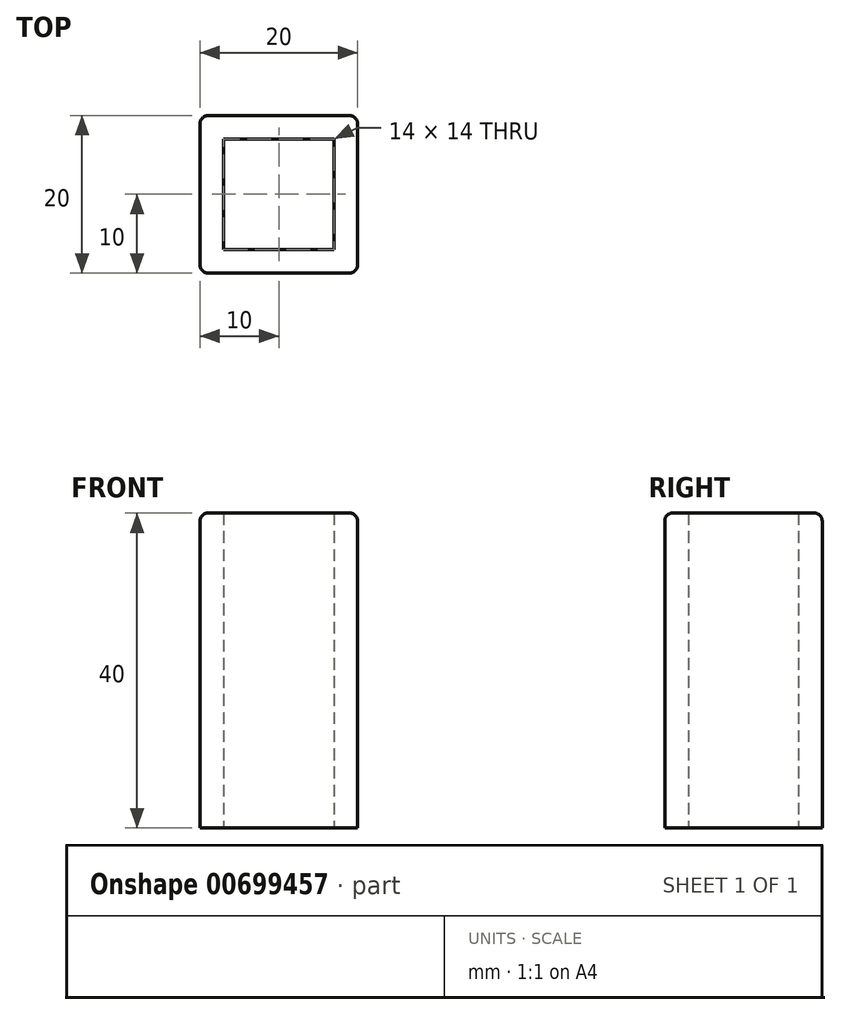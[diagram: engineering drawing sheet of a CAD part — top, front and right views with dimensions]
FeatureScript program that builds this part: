
annotation { "Feature Type Name" : "Feature", "Feature Type Description" : "" }
export const myFeature = defineFeature(function(context is Context, id is Id, definition is map)
    precondition{}
    {
        {
            var Q0;
            Q0=qCreatedBy(makeId("Top.planeOp"),FACE);
            var sketch = newSketch(context, id + "F0", { "sketchPlane" : qUnion([Q0])});
            skLineSegment(sketch, "E0.bottom", {"start": v(10, 10) * mm, "end": v(-10, 10) * mm});
            skLineSegment(sketch, "E0.top", {"start": v(10, -10) * mm, "end": v(-10, -10) * mm});
            skLineSegment(sketch, "E0.left", {"start": v(10, 10) * mm, "end": v(10, -10) * mm});
            skLineSegment(sketch, "E0.right", {"start": v(-10, 10) * mm, "end": v(-10, -10) * mm});
            skPoint(sketch, "E0.middle", {"position": v(0, 0) * mm});
            skLineSegment(sketch, "E1.0", {"start": v(7, -7) * mm, "end": v(-7, -7) * mm});
            skLineSegment(sketch, "E1.1", {"start": v(7, 7) * mm, "end": v(7, -7) * mm});
            skLineSegment(sketch, "E1.2", {"start": v(7, 7) * mm, "end": v(-7, 7) * mm});
            skLineSegment(sketch, "E1.3", {"start": v(-7, 7) * mm, "end": v(-7, -7) * mm});
            skSolve(sketch);
        }
        {
            var Q0;
            Q0=qSketchRegion(id+"F0",true);
            extrude(context, id + "F1", {"entities" : qUnion([Q0]), "depth" : 40 * mm, "offsetDistance" : 25 * mm});
        }
        {
            var Q0;
            Q0=makeQuery(id+"F1.opExtrude","SWEPT_EDGE",EDGE,{"disambiguationData":[OSD([sQuery(id+"F0.wireOp",EDGE,"E0.top"),sQuery(id+"F0.wireOp",EDGE,"E0.right")])]});
            var Q1;
            Q1=makeQuery(id+"F1.opExtrude","CAP_EDGE",EDGE,{"disambiguationData":[OSD([sQuery(id+"F0.wireOp",EDGE,"E0.top")])],"isStart":false});
            var Q2;
            Q2=makeQuery(id+"F1.opExtrude","CAP_EDGE",EDGE,{"disambiguationData":[OSD([sQuery(id+"F0.wireOp",EDGE,"E0.left")])],"isStart":false});
            var Q3;
            Q3=makeQuery(id+"F1.opExtrude","SWEPT_EDGE",EDGE,{"disambiguationData":[OSD([sQuery(id+"F0.wireOp",EDGE,"E0.top"),sQuery(id+"F0.wireOp",EDGE,"E0.left")])]});
            var Q4;
            Q4=makeQuery(id+"F1.opExtrude","SWEPT_EDGE",EDGE,{"disambiguationData":[OSD([sQuery(id+"F0.wireOp",EDGE,"E0.bottom"),sQuery(id+"F0.wireOp",EDGE,"E0.left")])]});
            var Q5;
            Q5=makeQuery(id+"F1.opExtrude","CAP_EDGE",EDGE,{"disambiguationData":[OSD([sQuery(id+"F0.wireOp",EDGE,"E0.bottom")])],"isStart":false});
            var Q6;
            Q6=makeQuery(id+"F1.opExtrude","CAP_EDGE",EDGE,{"disambiguationData":[OSD([sQuery(id+"F0.wireOp",EDGE,"E0.right")])],"isStart":false});
            var Q7;
            Q7=makeQuery(id+"F1.opExtrude","SWEPT_EDGE",EDGE,{"disambiguationData":[OSD([sQuery(id+"F0.wireOp",EDGE,"E0.bottom"),sQuery(id+"F0.wireOp",EDGE,"E0.right")])]});
            fillet(context, id + "F2", {"entities" : qUnion([Q0, Q1, Q2, Q3, Q4, Q5, Q6, Q7]), "radius" : 1 * mm, "tangentPropagation" : true, "allowEdgeOverflow" : false});
        }
    });
